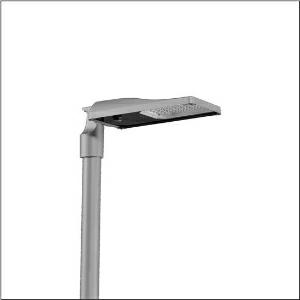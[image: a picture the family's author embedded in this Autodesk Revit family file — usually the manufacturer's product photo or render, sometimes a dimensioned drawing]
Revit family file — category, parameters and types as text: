
# Revit family: streetlight_sl_31_mini___st1_0a_5xh2d31r08ga_f9bd
name_source: partatom
category: Lighting Fixtures
units: mm (PartAtom-declared; Revit-internal decimal feet)

## family parameters
Cut with Voids When Loaded = No
Host = Face
Light Source = No
Part Type = Normal
Room Calculation Point = No
Round Connector Dimension = Use Diameter
Shared = No

## types (1)
- --- (1 x LED, 5880 lm, 39.3 W, 3000K)
    Apparent Load = 39 VA
    CIE Flux Codes = 37 72 97 100 100
    Color Rendering = 70
    Color Temperature = 3000K
    Default Elevation = 1800 mm
    Description = Streetlight SL 31 mini D4i, Desk-Remote mast luminaire for post-top, side-entry; light control with lens of PMMA; light distribution: ST1.0a, direct asymmetric distribution, for standard-compliant lighting for roads and squares; LED: luminous flux: 5.880lm, light colour: 730, colour temperature: 3000K; luminous efficacy: 149,6lm/W; control: pre-setting: logarithmic dimming characteristic, flexible luminous flux parameterisation, time-dependent luminous flux control, constant luminous flux control, power reduction, intelligent temperature release in ECG and LED module, overheat protection; luminaire housing, of diecast aluminium, Siteco® metallic grey (DB 702S), corrosivity category C5 high according to DIN EN ISO 12944; cover of toughened safety glass, transparent, mast flange of diecast aluminium, Siteco® metallic grey (DB 702S), spigot size: 76/60mm, mast flange included unmounted; with cable H07RN-F 2x 1.5mm², cable length: 6,5m, connection cable pre-assembled; mains connection: 220..240V, AC, 50/60Hz; power consumption (at start of service life): 39,3W / (at end of service life): 40,7W / (with reduced operation 50%): 18,1W; protection rating (complete): IP66; insulation class (complete): insulation class II (safety insulation); impact resistance: IK09; certification: CE, ENEC, ENEC+, VDE, UKCA, ZD4i; permissible operating ambient temperature for outdoor applications: -40..+50°C; packaging unit: 1 piece

Light Distribution: ST1.0a
    Height = 76 mm
    Lamp = 1 x LED
    Lamp Light Flux = 5880 lm
    Lamp Power = 39.3 W
    Lamp count = 1
    Length = 547 mm
    Luminous efficacy = 150 lm/W
    Manufacturer = Siteco
    ModVariant = No
    Model = 5XH2D31R08GA
    Number of Poles = 1
    OnlyDefault = Yes
    Power Factor = 1
    Product Name = Streetlight SL 31 mini | ST1.0a
    Product group = mast luminaire | pylon top
    ProductGroupID = 6100
    Protection Class = Protection class II
    Protection Degree = IP 66
    RLX_Detail_Level = 1
    RLX_Emergency_Light_Flux = 0 lm
    RLX_Emergency_Type = 0
    RLX_Emergency_Type_DB = No
    RlxData = <blob elided: 39605 chars, md5=b0e14ed8>
    Socket = socket
    Standby Power = 0 W
    System Light Flux = 5880 lm
    System Power = 39 W
    Type Comments = factory setting: luminous flux: 100 % | dim-lin: 254 | 798 mA
    Type Image = l_1300328.jpg
    URL = http://relux.com
    VarID = @adj_054904
    Voltage = 0 V
    Weight = 0.00 kg
    Width = 265 mm

## geometry (parser evidence)
native form markers: Blend x4, Sweep x10
no freeform markers — native parametric forms only
